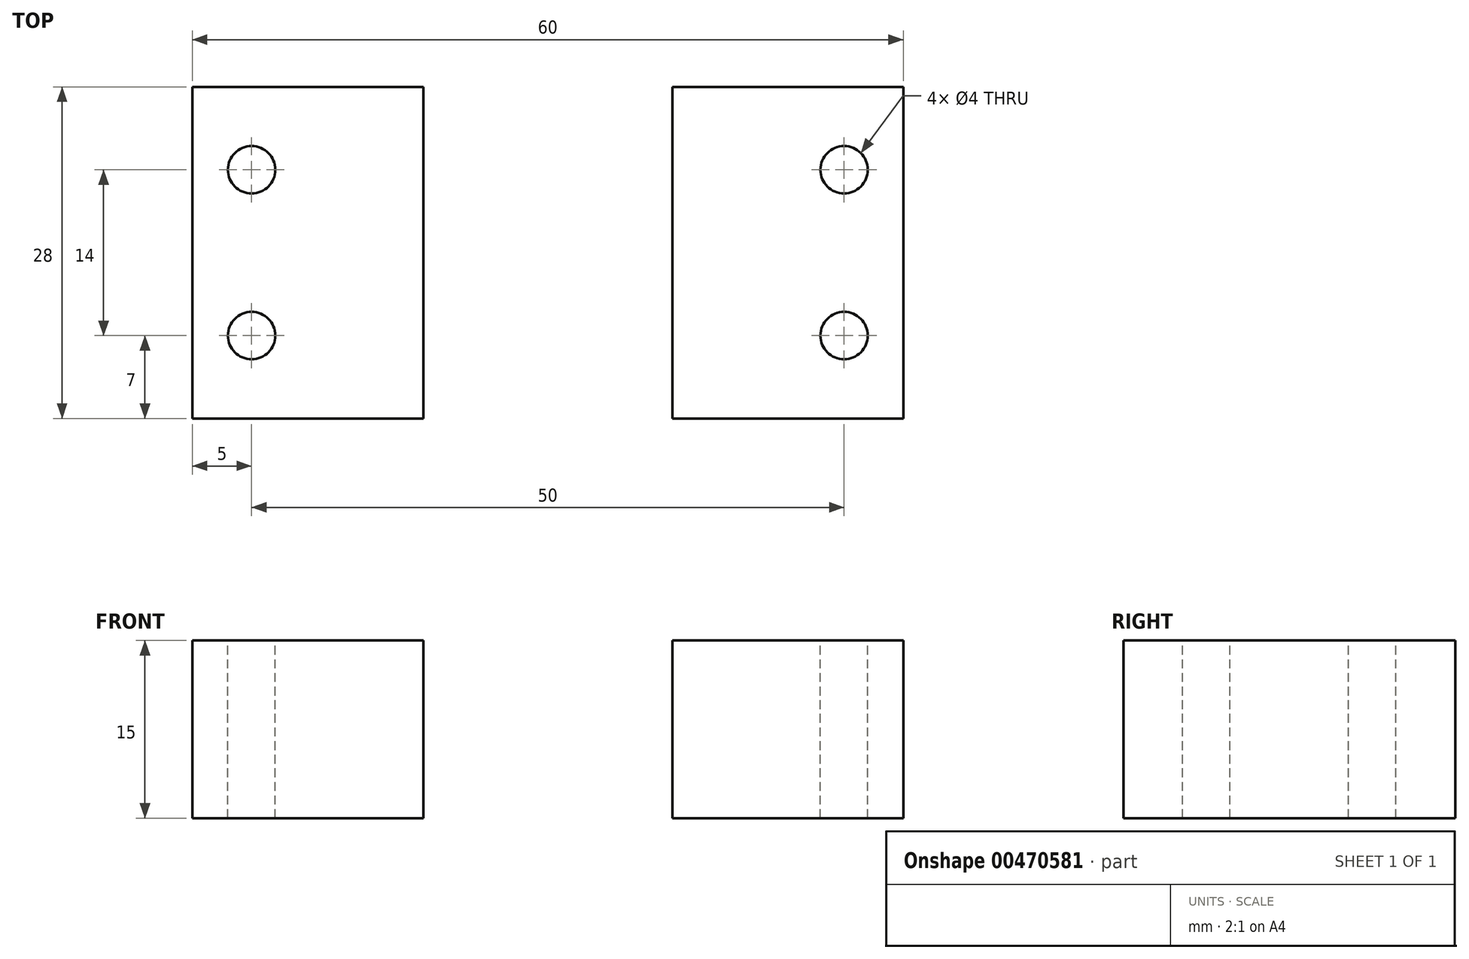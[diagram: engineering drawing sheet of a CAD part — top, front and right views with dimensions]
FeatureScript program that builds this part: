
annotation { "Feature Type Name" : "Feature", "Feature Type Description" : "" }
export const myFeature = defineFeature(function(context is Context, id is Id, definition is map)
    precondition{}
    {
        {
            var Q0;
            Q0=qCreatedBy(makeId("Top.planeOp"),FACE);
            var sketch = newSketch(context, id + "F0", { "sketchPlane" : qUnion([Q0])});
            skLineSegment(sketch, "E0.bottom", {"start": v(25, -7) * mm, "end": v(-25, -7) * mm, "construction": true});
            skLineSegment(sketch, "E0.top", {"start": v(25, 7) * mm, "end": v(-25, 7) * mm, "construction": true});
            skLineSegment(sketch, "E0.left", {"start": v(25, -7) * mm, "end": v(25, 7) * mm, "construction": true});
            skLineSegment(sketch, "E0.right", {"start": v(-25, -7) * mm, "end": v(-25, 7) * mm, "construction": true});
            skPoint(sketch, "E0.middle", {"position": v(0, 0) * mm});
            skLineSegment(sketch, "E1.bottom", {"start": v(30, -14) * mm, "end": v(-30, -14) * mm});
            skLineSegment(sketch, "E1.top", {"start": v(30, 14) * mm, "end": v(-30, 14) * mm});
            skLineSegment(sketch, "E1.left", {"start": v(30, -14) * mm, "end": v(30, 14) * mm});
            skLineSegment(sketch, "E1.right", {"start": v(-30, -14) * mm, "end": v(-30, 14) * mm});
            skLineSegment(sketch, "E2.bottom", {"start": v(10.5, -14) * mm, "end": v(-10.5, -14) * mm});
            skLineSegment(sketch, "E2.top", {"start": v(10.5, 14) * mm, "end": v(-10.5, 14) * mm});
            skLineSegment(sketch, "E2.left", {"start": v(10.5, -14) * mm, "end": v(10.5, 14) * mm});
            skLineSegment(sketch, "E2.right", {"start": v(-10.5, -14) * mm, "end": v(-10.5, 14) * mm});
            skCircle(sketch, "E3", {"center": v(25, 7) * mm, "radius": 2 * mm});
            skCircle(sketch, "E4", {"center": v(25, -7) * mm, "radius": 2 * mm});
            skCircle(sketch, "E5", {"center": v(-25, -7) * mm, "radius": 2 * mm});
            skCircle(sketch, "E6", {"center": v(-25, 7) * mm, "radius": 2 * mm});
            skSolve(sketch);
        }
        {
            var Q0;
            {var subQ1=sQuery(id+"F0.wireOp",EDGE,"E1.left");Q0=makeQuery(id+"F0.imprint","IMPRINT",FACE,{"disambiguationData":[TD([[makeQuery(id+"F0.imprint","IMPRINT",EDGE,{"derivedFrom":subQ1}),1.0]])]});}
            var Q1;
            Q1=makeQuery(id+"F0.imprint","IMPRINT",FACE,{"disambiguationData":[TD([[makeQuery(id+"F0.imprint","IMPRINT",EDGE,{"derivedFrom":sQuery(id+"F0.wireOp",EDGE,"E2.bottom")}),-1.0]])]});
            var Q2;
            {var subQ1=sQuery(id+"F0.wireOp",EDGE,"E1.right");Q2=makeQuery(id+"F0.imprint","IMPRINT",FACE,{"disambiguationData":[TD([[makeQuery(id+"F0.imprint","IMPRINT",EDGE,{"derivedFrom":subQ1}),-1.0]])]});}
            extrude(context, id + "F1", {"entities" : qUnion([Q0, Q1, Q2]), "oppositeDirection" : true, "depth" : 5 * mm});
        }
        {
            var Q0;
            {var subQ1=sQuery(id+"F0.wireOp",EDGE,"E1.right");Q0=makeQuery(id+"F0.imprint","IMPRINT",FACE,{"disambiguationData":[TD([[makeQuery(id+"F0.imprint","IMPRINT",EDGE,{"derivedFrom":subQ1}),-1.0]])]});}
            var Q1;
            {var subQ1=sQuery(id+"F0.wireOp",EDGE,"E1.left");Q1=makeQuery(id+"F0.imprint","IMPRINT",FACE,{"disambiguationData":[TD([[makeQuery(id+"F0.imprint","IMPRINT",EDGE,{"derivedFrom":subQ1}),1.0]])]});}
            extrude(context, id + "F2", {"entities" : qUnion([Q0, Q1]), "operationType" : NewBodyOperationType.ADD, "depth" : 10 * mm});
        }
    });
